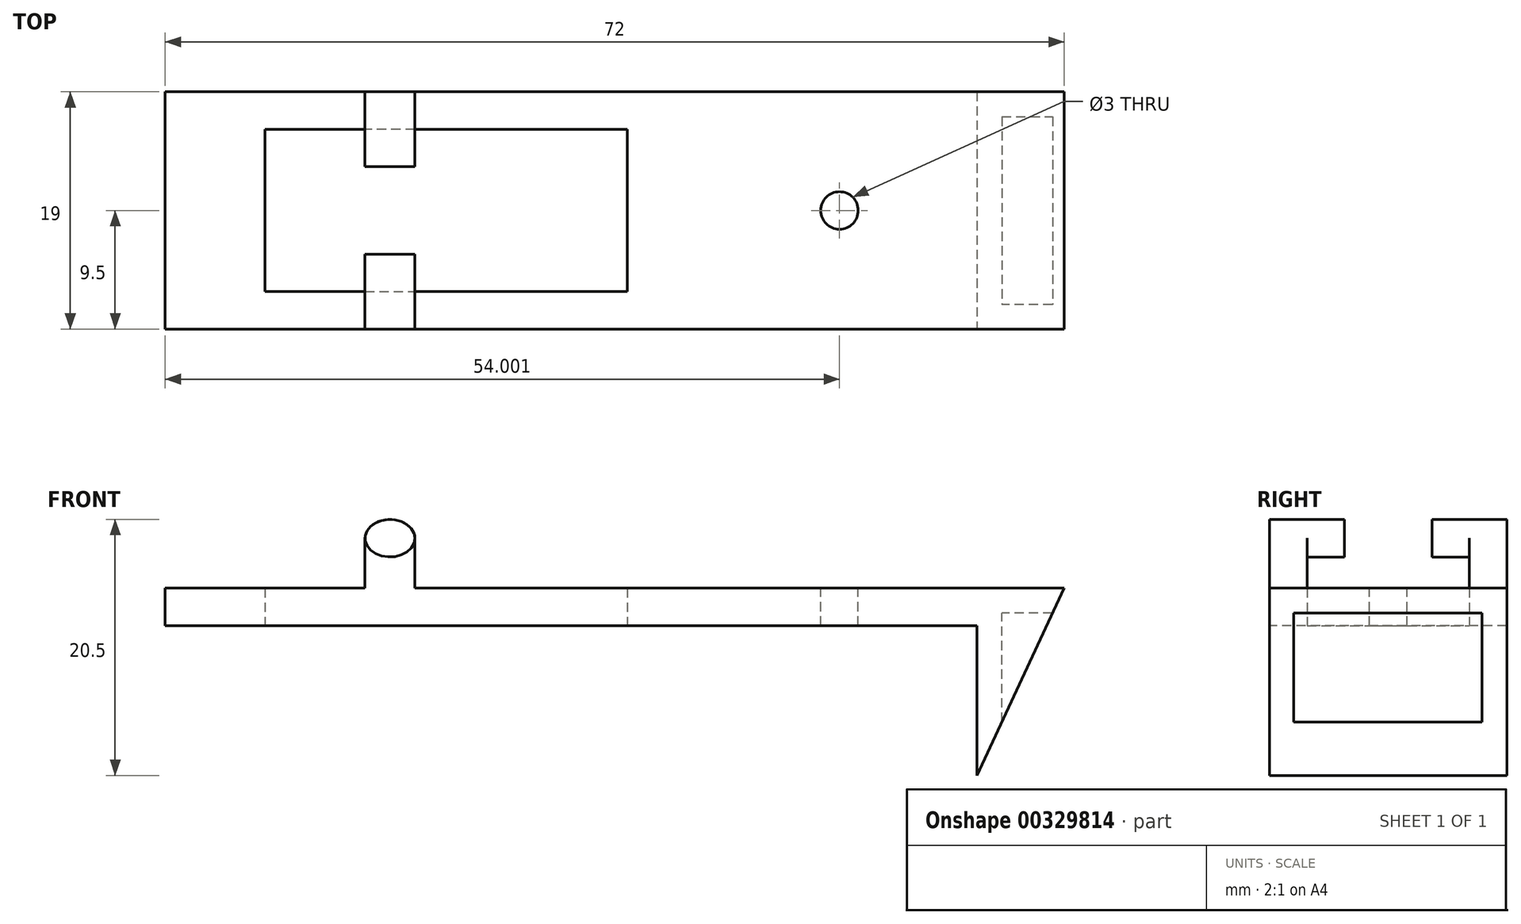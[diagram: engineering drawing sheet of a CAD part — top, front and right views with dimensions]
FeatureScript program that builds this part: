
annotation { "Feature Type Name" : "Feature", "Feature Type Description" : "" }
export const myFeature = defineFeature(function(context is Context, id is Id, definition is map)
    precondition{}
    {
        {
            var Q0;
            Q0=qCreatedBy(makeId("Front.planeOp"),FACE);
            var sketch = newSketch(context, id + "F0", { "sketchPlane" : qUnion([Q0])});
            skLineSegment(sketch, "E0.bottom", {"start": v(-33.88, 0) * mm, "end": v(38.12, 0) * mm});
            skLineSegment(sketch, "E0.top", {"start": v(-33.88, -3) * mm, "end": v(38.12, -3) * mm});
            skLineSegment(sketch, "E0.left", {"start": v(-33.88, 0) * mm, "end": v(-33.88, -3) * mm});
            skLineSegment(sketch, "E0.right", {"start": v(38.12, 0) * mm, "end": v(38.12, -3) * mm});
            skSolve(sketch);
        }
        {
            var Q0;
            Q0 = qSketchRegion(id + "F0", true);
            extrude(context, id + "F1", {"entities" : qUnion([Q0]), "depth" : 19 * mm});
        }
        {
            var Q0;
            Q0=makeQuery(id+"F1.opExtrude","SWEPT_FACE",FACE,{"disambiguationData":[OSD([sQuery(id+"F0.wireOp",EDGE,"E0.bottom")])]});
            var sketch = newSketch(context, id + "F2", { "sketchPlane" : qUnion([Q0])});
            skLineSegment(sketch, "E1", {"start": v(-25.88, -3) * mm, "end": v(-25.88, -16) * mm});
            skLineSegment(sketch, "E2.0", {"start": v(-25.88, -3) * mm, "end": v(3.12, -3) * mm});
            skLineSegment(sketch, "E3.0", {"start": v(-25.88, -16) * mm, "end": v(3.12, -16) * mm});
            skLineSegment(sketch, "E4.0", {"start": v(3.12, -3) * mm, "end": v(3.12, -16) * mm});
            skSolve(sketch);
        }
        {
            var Q0;
            Q0 = qSketchRegion(id + "F2", true);
            extrude(context, id + "F3", {"entities" : qUnion([Q0]), "operationType" : NewBodyOperationType.REMOVE, "endBound" : BoundingType.SYMMETRIC, "depth" : 25 * mm});
        }
        {
            var Q0;
            Q0=qCreatedBy(makeId("Right.planeOp"),FACE);
            var Q1;
            Q1=makeQuery(id+"F1.opExtrude","CAP_VERTEX",VERTEX,{"disambiguationData":[OSD([sQuery(id+"F0.wireOp",EDGE,"E0.top"),sQuery(id+"F0.wireOp",EDGE,"E0.right")])],"isStart":false});
            cPlane(context, id + "F4", {"entities" : qUnion([Q0, Q1]), "cplaneType" : CPlaneType.PLANE_POINT, "offset" : 25 * mm, "width" : 150 * mm, "height" : 150 * mm});
        }
        {
            var Q0;
            Q0=qCreatedBy(id+"F4.planeOp",FACE);
            cPlane(context, id + "F5", {"entities" : qUnion([Q0]), "cplaneType" : CPlaneType.OFFSET, "offset" : 5 * mm, "oppositeDirection" : true, "width" : 150 * mm, "height" : 150 * mm});
        }
        {
            var Q0;
            Q0=makeQuery(id+"F1.opExtrude","CAP_FACE",FACE,{"disambiguationData":[OSD([sQuery(id+"F0.wireOp",EDGE,"E0.bottom"),sQuery(id+"F0.wireOp",EDGE,"E0.top"),sQuery(id+"F0.wireOp",EDGE,"E0.left"),sQuery(id+"F0.wireOp",EDGE,"E0.right")])],"isStart":false});
            var sketch = newSketch(context, id + "F6", { "sketchPlane" : qUnion([Q0])});
            skLineSegment(sketch, "E5", {"start": v(38.12, 0) * mm, "end": v(31.12, 0) * mm});
            skLineSegment(sketch, "E6", {"start": v(31.12, 0) * mm, "end": v(31.12, -15) * mm});
            skLineSegment(sketch, "E7", {"start": v(31.12, -15) * mm, "end": v(38.12, 0) * mm});
            skLineSegment(sketch, "E8", {"start": v(38.12, 0) * mm, "end": v(42.23, 0) * mm});
            skLineSegment(sketch, "E9", {"start": v(42.23, 0) * mm, "end": v(42.23, -15.89) * mm});
            skLineSegment(sketch, "E10", {"start": v(42.23, -15.89) * mm, "end": v(31.12, -15) * mm});
            skSolve(sketch);
        }
        {
            var Q0;
            {var subQ0=sQuery(id+"F6.wireOp",EDGE,"E5");Q0=makeQuery(id+"F6.imprint","IMPRINT",FACE,{"disambiguationData":[TD([[makeQuery(id+"F6.imprint","IMPRINT",EDGE,{"derivedFrom":subQ0}),-1.0]])]});}
            var Q1;
            {var subQ1=sQuery(id+"F6.wireOp",EDGE,"E6");var subQ3=makeQuery(id+"F1.opExtrude","CAP_EDGE",EDGE,{"disambiguationData":[OSD([sQuery(id+"F0.wireOp",EDGE,"E0.top")])],"isStart":false});var subQ4=makeQuery(id+"F6.imprint","INTERSECT",VERTEX,{"derivedFrom":[subQ3,subQ1]});Q1=makeQuery(id+"F6.imprint","IMPRINT",FACE,{"disambiguationData":[TD([[makeQuery(id+"F6.imprint","IMPRINT",EDGE,{"disambiguationData":[TD([[subQ4,-1.0]])],"derivedFrom":subQ3}),-1.0]])]});}
            extrude(context, id + "F7", {"entities" : qUnion([Q0, Q1]), "operationType" : NewBodyOperationType.ADD, "oppositeDirection" : true, "depth" : 19 * mm});
        }
        {
            var Q0;
            {var subQ1=makeQuery(id+"F1.opExtrude","CAP_EDGE",EDGE,{"disambiguationData":[OSD([sQuery(id+"F0.wireOp",EDGE,"E0.right")])],"isStart":false});Q0=makeQuery(id+"F6.imprint","IMPRINT",FACE,{"disambiguationData":[TD([[makeQuery(id+"F6.imprint","IMPRINT",EDGE,{"derivedFrom":subQ1}),-1.0]])]});}
            var Q1;
            Q1=makeQuery(id+"F6.imprint","IMPRINT",FACE,{"disambiguationData":[TD([[makeQuery(id+"F6.imprint","IMPRINT",EDGE,{"derivedFrom":sQuery(id+"F6.wireOp",EDGE,"E8")}),-1.0]])]});
            extrude(context, id + "F8", {"entities" : qUnion([Q0, Q1]), "operationType" : NewBodyOperationType.REMOVE, "endBound" : BoundingType.SYMMETRIC, "oppositeDirection" : true, "depth" : 40 * mm});
        }
        {
            var Q0;
            Q0=qCreatedBy(id+"F5.planeOp",FACE);
            var sketch = newSketch(context, id + "F9", { "sketchPlane" : qUnion([Q0])});
            skLineSegment(sketch, "E11", {"start": v(-2, -19.44) * mm, "end": v(-17.05, -19.44) * mm});
            skLineSegment(sketch, "E12.0", {"start": v(-17.05, -2) * mm, "end": v(-2, -2) * mm});
            skLineSegment(sketch, "E13.0", {"start": v(-17.05, -19.44) * mm, "end": v(-17.05, -2) * mm});
            skLineSegment(sketch, "E14.0", {"start": v(-2, -2) * mm, "end": v(-2, -19.44) * mm});
            skSolve(sketch);
        }
        {
            var Q0;
            Q0 = qSketchRegion(id + "F9", true);
            extrude(context, id + "F10", {"entities" : qUnion([Q0]), "operationType" : NewBodyOperationType.REMOVE, "depth" : 25 * mm});
        }
        {
            var Q0;
            Q0=makeQuery(id+"F1.opExtrude","SWEPT_FACE",FACE,{"disambiguationData":[OSD([sQuery(id+"F0.wireOp",EDGE,"E0.bottom")])]});
            var sketch = newSketch(context, id + "F11", { "sketchPlane" : qUnion([Q0])});
            skLineSegment(sketch, "E15", {"start": v(3.12, -3) * mm, "end": v(3.12, 12.94) * mm});
            skLineSegment(sketch, "E16.0", {"start": v(20.12, -31.1) * mm, "end": v(20.12, 12.94) * mm});
            skLineSegment(sketch, "E17", {"start": v(3.12, -3) * mm, "end": v(20.12, -3) * mm});
            skLineSegment(sketch, "E18.0", {"start": v(3.12, -9.5) * mm, "end": v(20.12, -9.5) * mm});
            skCircle(sketch, "E19", {"center": v(20.12, -9.5) * mm, "radius": 1.5 * mm});
            skSolve(sketch);
        }
        {
            var Q0;
            {var subQ0=sQuery(id+"F11.wireOp",EDGE,"E18.0");var subQ1=sQuery(id+"F11.wireOp",EDGE,"E16.0");var subQ2=makeQuery(id+"F11.imprint","INTERSECT",VERTEX,{"derivedFrom":[subQ1,subQ0]});Q0=makeQuery(id+"F11.imprint","IMPRINT",FACE,{"disambiguationData":[TD([[makeQuery(id+"F11.imprint","IMPRINT",EDGE,{"disambiguationData":[TD([[subQ2,-1.0]])],"derivedFrom":subQ1}),1.0]])]});}
            var Q1;
            {var subQ0=sQuery(id+"F11.wireOp",EDGE,"E16.0");var subQ1=makeQuery(id+"F11.imprint","INTERSECT",VERTEX,{"derivedFrom":[subQ0,sQuery(id+"F11.wireOp",EDGE,"E18.0")]});Q1=makeQuery(id+"F11.imprint","IMPRINT",FACE,{"disambiguationData":[TD([[makeQuery(id+"F11.imprint","IMPRINT",EDGE,{"disambiguationData":[TD([[subQ1,1.0]])],"derivedFrom":subQ0}),-1.0]])]});}
            var Q2;
            {var subQ0=sQuery(id+"F11.wireOp",EDGE,"E18.0");var subQ1=sQuery(id+"F11.wireOp",EDGE,"E16.0");var subQ2=makeQuery(id+"F11.imprint","INTERSECT",VERTEX,{"derivedFrom":[subQ1,subQ0]});Q2=makeQuery(id+"F11.imprint","IMPRINT",FACE,{"disambiguationData":[TD([[makeQuery(id+"F11.imprint","IMPRINT",EDGE,{"disambiguationData":[TD([[subQ2,1.0]])],"derivedFrom":subQ1}),1.0]])]});}
            extrude(context, id + "F12", {"entities" : qUnion([Q0, Q1, Q2]), "operationType" : NewBodyOperationType.REMOVE, "endBound" : BoundingType.SYMMETRIC, "oppositeDirection" : true, "depth" : 25 * mm});
        }
        {
            var Q0;
            Q0=makeQuery(id+"F7.boolean.opBoolean","MERGE",FACE,{"derivedFrom":[makeQuery(id+"F1.opExtrude","CAP_FACE",FACE,{"disambiguationData":[OSD([sQuery(id+"F0.wireOp",EDGE,"E0.bottom"),sQuery(id+"F0.wireOp",EDGE,"E0.top"),sQuery(id+"F0.wireOp",EDGE,"E0.left"),sQuery(id+"F0.wireOp",EDGE,"E0.right")])],"isStart":false}),makeQuery(id+"F7.opExtrude","CAP_FACE",FACE,{"disambiguationData":[OSD([sQuery(id+"F6.wireOp",EDGE,"E5"),sQuery(id+"F6.wireOp",EDGE,"E6"),sQuery(id+"F6.wireOp",EDGE,"E7")])],"isStart":true})]});
            var sketch = newSketch(context, id + "F13", { "sketchPlane" : qUnion([Q0])});
            skLineSegment(sketch, "E20", {"start": v(-33.88, 0) * mm, "end": v(-33.88, 18.82) * mm});
            skLineSegment(sketch, "E21.0", {"start": v(-17.88, 0) * mm, "end": v(-17.88, 18.82) * mm});
            skLineSegment(sketch, "E22.0", {"start": v(-13.88, 0) * mm, "end": v(-13.88, 18.82) * mm});
            skLineSegment(sketch, "E23", {"start": v(-17.88, 0) * mm, "end": v(-13.88, 0) * mm});
            skLineSegment(sketch, "E24.0", {"start": v(-17.88, 4) * mm, "end": v(-13.88, 4) * mm});
            skEllipse(sketch, "E25", {"center": v(-15.88, 4) * mm, "majorRadius": 2 * mm, "minorRadius": 1.5 * mm, "majorAxis": v(1, 0)});
            skSolve(sketch);
        }
        {
            var Q0;
            {var subQ0=sQuery(id+"F13.wireOp",EDGE,"E23");Q0=makeQuery(id+"F13.imprint","IMPRINT",FACE,{"disambiguationData":[TD([[makeQuery(id+"F13.imprint","IMPRINT",EDGE,{"derivedFrom":subQ0}),1.0]])]});}
            extrude(context, id + "F14", {"entities" : qUnion([Q0]), "operationType" : NewBodyOperationType.ADD, "oppositeDirection" : true, "depth" : 3 * mm});
        }
        {
            var Q0;
            {var subQ0=sQuery(id+"F13.wireOp",EDGE,"E24.0");Q0=makeQuery(id+"F13.imprint","IMPRINT",FACE,{"disambiguationData":[TD([[makeQuery(id+"F13.imprint","IMPRINT",EDGE,{"derivedFrom":subQ0}),-1.0]])]});}
            var Q1;
            {var subQ0=sQuery(id+"F13.wireOp",EDGE,"E24.0");Q1=makeQuery(id+"F13.imprint","IMPRINT",FACE,{"disambiguationData":[TD([[makeQuery(id+"F13.imprint","IMPRINT",EDGE,{"derivedFrom":subQ0}),1.0]])]});}
            extrude(context, id + "F15", {"entities" : qUnion([Q0, Q1]), "operationType" : NewBodyOperationType.ADD, "oppositeDirection" : true, "depth" : 6 * mm});
        }
        {
            var Q0;
            Q0=makeQuery(id+"F7.boolean.opBoolean","MERGE",FACE,{"derivedFrom":[makeQuery(id+"F1.opExtrude","CAP_FACE",FACE,{"disambiguationData":[OSD([sQuery(id+"F0.wireOp",EDGE,"E0.bottom"),sQuery(id+"F0.wireOp",EDGE,"E0.top"),sQuery(id+"F0.wireOp",EDGE,"E0.left"),sQuery(id+"F0.wireOp",EDGE,"E0.right")])],"isStart":true}),makeQuery(id+"F7.opExtrude","CAP_FACE",FACE,{"disambiguationData":[OSD([sQuery(id+"F6.wireOp",EDGE,"E5"),sQuery(id+"F6.wireOp",EDGE,"E6"),sQuery(id+"F6.wireOp",EDGE,"E7")])],"isStart":false})]});
            var sketch = newSketch(context, id + "F16", { "sketchPlane" : qUnion([Q0])});
            skLineSegment(sketch, "E26.0", {"start": v(13.88, 0) * mm, "end": v(13.88, 18.82) * mm});
            skLineSegment(sketch, "E27.0", {"start": v(17.88, 0) * mm, "end": v(17.88, 18.82) * mm});
            skLineSegment(sketch, "E28", {"start": v(13.88, 0) * mm, "end": v(17.88, 0) * mm});
            skEllipse(sketch, "E29", {"center": v(15.88, 4) * mm, "majorRadius": 2 * mm, "minorRadius": 1.5 * mm, "majorAxis": v(1, 0)});
            skSolve(sketch);
        }
        {
            var Q0;
            {var subQ0=sQuery(id+"F16.wireOp",EDGE,"E28");Q0=makeQuery(id+"F16.imprint","IMPRINT",FACE,{"disambiguationData":[TD([[makeQuery(id+"F16.imprint","IMPRINT",EDGE,{"derivedFrom":subQ0}),-1.0]])]});}
            extrude(context, id + "F17", {"entities" : qUnion([Q0]), "operationType" : NewBodyOperationType.ADD, "oppositeDirection" : true, "depth" : 3 * mm});
        }
        {
            var Q0;
            {var subQ0=sQuery(id+"F16.wireOp",EDGE,"E29");var subQ1=makeQuery(id+"F16.imprint","INTERSECT",VERTEX,{"derivedFrom":[sQuery(id+"F16.wireOp",EDGE,"E26.0"),subQ0]});Q0=makeQuery(id+"F16.imprint","IMPRINT",FACE,{"disambiguationData":[TD([[makeQuery(id+"F16.imprint","IMPRINT",EDGE,{"disambiguationData":[TD([[subQ1,1.0]])],"derivedFrom":subQ0}),1.0]])]});}
            extrude(context, id + "F18", {"entities" : qUnion([Q0]), "operationType" : NewBodyOperationType.ADD, "oppositeDirection" : true, "depth" : 6 * mm});
        }
    });
